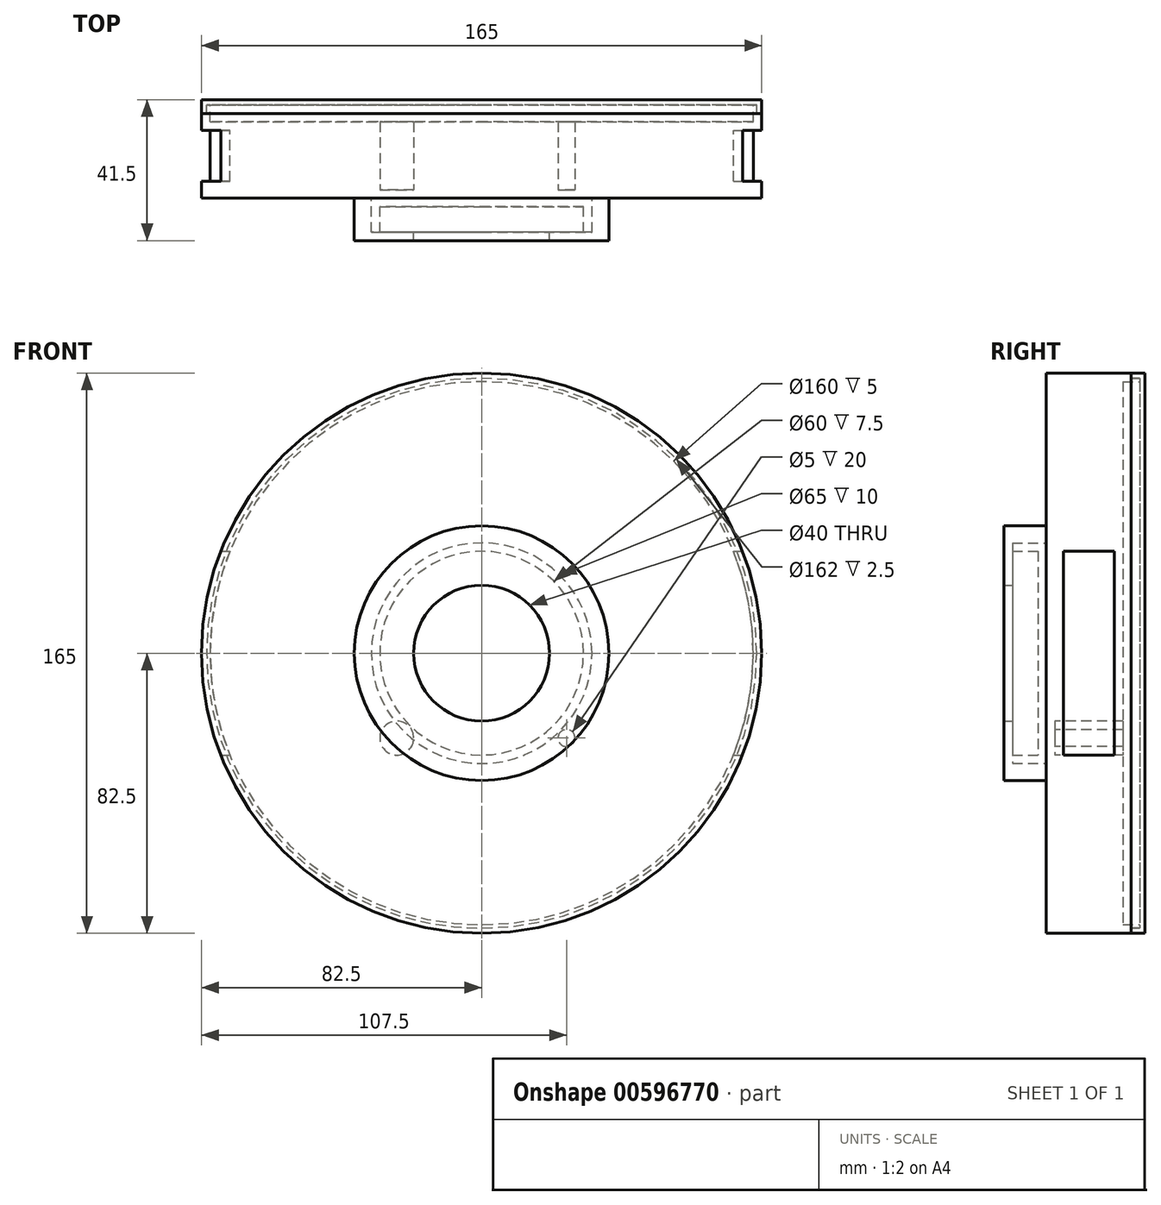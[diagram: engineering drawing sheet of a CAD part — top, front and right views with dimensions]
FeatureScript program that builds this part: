
annotation { "Feature Type Name" : "Feature", "Feature Type Description" : "" }
export const myFeature = defineFeature(function(context is Context, id is Id, definition is map)
    precondition{}
    {
        {
            var Q0;
            Q0=qCreatedBy(makeId("Right.planeOp"),FACE);
            var sketch = newSketch(context, id + "F0", { "sketchPlane" : qUnion([Q0])});
            skLineSegment(sketch, "E0.bottom", {"start": v(0, 0) * mm, "end": v(-2.5, 0) * mm});
            skLineSegment(sketch, "E0.top", {"start": v(0, 32.5) * mm, "end": v(-10, 32.5) * mm});
            skLineSegment(sketch, "E1", {"start": v(0, 0) * mm, "end": v(-55.69, 0) * mm, "construction": true});
            skLineSegment(sketch, "E2", {"start": v(-2.5, 0) * mm, "end": v(-2.5, 30) * mm});
            skLineSegment(sketch, "E3", {"start": v(-2.5, 30) * mm, "end": v(-10, 30) * mm});
            skLineSegment(sketch, "E4", {"start": v(-10, 30) * mm, "end": v(-10, 32.5) * mm});
            skLineSegment(sketch, "E5", {"start": v(0, 32.5) * mm, "end": v(0, 82.5) * mm});
            skLineSegment(sketch, "E6", {"start": v(0, 82.5) * mm, "end": v(25, 82.5) * mm});
            skLineSegment(sketch, "E7", {"start": v(25, 80) * mm, "end": v(2.5, 80) * mm});
            skLineSegment(sketch, "E8", {"start": v(2.5, 80) * mm, "end": v(2.5, 0) * mm});
            skLineSegment(sketch, "E9", {"start": v(2.5, 0) * mm, "end": v(-2.5, 0) * mm});
            skLineSegment(sketch, "E10", {"start": v(25, 80) * mm, "end": v(27.5, 80) * mm});
            skLineSegment(sketch, "E11", {"start": v(27.5, 80) * mm, "end": v(27.5, 81) * mm});
            skLineSegment(sketch, "E12", {"start": v(27.5, 81) * mm, "end": v(25, 81) * mm});
            skLineSegment(sketch, "E13", {"start": v(25, 81) * mm, "end": v(25, 82.5) * mm});
            skSolve(sketch);
        }
        {
            var Q0;
            Q0=qCreatedBy(makeId("Right.planeOp"),FACE);
            var sketch = newSketch(context, id + "F1", { "sketchPlane" : qUnion([Q0])});
            skLineSegment(sketch, "E14", {"start": v(0, 32.5) * mm, "end": v(-10, 32.5) * mm});
            skLineSegment(sketch, "E15", {"start": v(-10, 32.5) * mm, "end": v(-10, 20) * mm});
            skLineSegment(sketch, "E16", {"start": v(-10, 20) * mm, "end": v(-12.5, 20) * mm});
            skLineSegment(sketch, "E17", {"start": v(-12.5, 20) * mm, "end": v(-12.5, 37.5) * mm});
            skLineSegment(sketch, "E18", {"start": v(-12.5, 37.5) * mm, "end": v(0, 37.5) * mm});
            skLineSegment(sketch, "E19", {"start": v(0, 37.5) * mm, "end": v(0, 32.5) * mm});
            skLineSegment(sketch, "E20", {"start": v(0, 0) * mm, "end": v(-84.01, 0) * mm, "construction": true});
            skSolve(sketch);
        }
        {
            var Q0;
            Q0=qCreatedBy(makeId("Right.planeOp"),FACE);
            var sketch = newSketch(context, id + "F2", { "sketchPlane" : qUnion([Q0])});
            skLineSegment(sketch, "E21.bottom", {"start": v(-2.5, 0) * mm, "end": v(-10, 0) * mm});
            skLineSegment(sketch, "E21.top", {"start": v(-2.5, 30) * mm, "end": v(-10, 30) * mm});
            skLineSegment(sketch, "E21.left", {"start": v(-2.5, 0) * mm, "end": v(-2.5, 30) * mm});
            skLineSegment(sketch, "E21.right", {"start": v(-10, 0) * mm, "end": v(-10, 30) * mm});
            skSolve(sketch);
        }
        {
            var Q0;
            Q0=qCreatedBy(makeId("Right.planeOp"),FACE);
            var sketch = newSketch(context, id + "F3", { "sketchPlane" : qUnion([Q0])});
            skLineSegment(sketch, "E22", {"start": v(27.5, 0) * mm, "end": v(27.5, 79.3) * mm});
            skLineSegment(sketch, "E23", {"start": v(27.5, 79.3) * mm, "end": v(27.5, 81) * mm});
            skLineSegment(sketch, "E24", {"start": v(25, 82.5) * mm, "end": v(25, 81) * mm});
            skLineSegment(sketch, "E25", {"start": v(25, 81) * mm, "end": v(27.5, 81) * mm});
            skLineSegment(sketch, "E26", {"start": v(25, 82.5) * mm, "end": v(29, 82.5) * mm});
            skLineSegment(sketch, "E27", {"start": v(29, 82.5) * mm, "end": v(29, 0) * mm});
            skLineSegment(sketch, "E28", {"start": v(0, 0) * mm, "end": v(36.98, 0) * mm, "construction": true});
            skLineSegment(sketch, "E29", {"start": v(27.5, 0) * mm, "end": v(29, 0) * mm});
            skSolve(sketch);
        }
        {
            var Q0;
            Q0=makeQuery(id+"F0.imprint","IMPRINT",FACE,{"disambiguationData":[TD([[makeQuery(id+"F0.imprint","IMPRINT",EDGE,{"derivedFrom":sQuery(id+"F0.wireOp",EDGE,"E0.top")}),1.0]])]});
            var Q1;
            Q1=sQuery(id+"F0.wireOp",EDGE,"E0.top");
            var Q2;
            Q2=sQuery(id+"F0.wireOp",EDGE,"E0.bottom");
            var Q3;
            Q3=sQuery(id+"F0.wireOp",EDGE,"E0.right");
            var Q4;
            Q4=sQuery(id+"F0.wireOp",EDGE,"E0.left");
            var Q5;
            Q5=sQuery(id+"F0.wireOp",EDGE,"E1");
            revolve(context, id + "F4", {"entities" : qUnion([Q0]), "surfaceEntities" : qUnion([Q1, Q2, Q3, Q4]), "axis" : qUnion([Q5]), "revolveType" : RevolveType.FULL});
        }
        {
            var Q0;
            Q0=makeQuery(id+"F1.imprint","IMPRINT",FACE,{"disambiguationData":[TD([[makeQuery(id+"F1.imprint","IMPRINT",EDGE,{"derivedFrom":sQuery(id+"F1.wireOp",EDGE,"E14")}),-1.0]])]});
            var Q1;
            Q1=sQuery(id+"F1.wireOp",EDGE,"E20");
            revolve(context, id + "F5", {"entities" : qUnion([Q0]), "axis" : qUnion([Q1]), "revolveType" : RevolveType.FULL});
        }
        {
            var Q0;
            Q0 = qSketchRegion(id + "F3", true);
            var Q1;
            Q1=sQuery(id+"F3.wireOp",EDGE,"E27");
            var Q2;
            Q2=sQuery(id+"F3.wireOp",EDGE,"E22");
            var Q3;
            Q3=sQuery(id+"F3.wireOp",EDGE,"E26");
            var Q4;
            Q4=sQuery(id+"F3.wireOp",EDGE,"E25");
            var Q5;
            Q5=sQuery(id+"F3.wireOp",EDGE,"E24");
            var Q6;
            Q6=sQuery(id+"F3.wireOp",EDGE,"E23");
            var Q7;
            Q7=sQuery(id+"F3.wireOp",EDGE,"E28");
            revolve(context, id + "F6", {"entities" : qUnion([Q0]), "surfaceEntities" : qUnion([Q1, Q2, Q3, Q4, Q5, Q6]), "axis" : qUnion([Q7]), "revolveType" : RevolveType.FULL});
        }
        {
            var Q0;
            Q0 = qSketchRegion(id + "F2", true);
            var Q1;
            Q1=sQuery(id+"F0.wireOp",EDGE,"E1");
            revolve(context, id + "F7", {"entities" : qUnion([Q0]), "axis" : qUnion([Q1]), "revolveType" : RevolveType.FULL});
        }
        {
            var Q0;
            Q0=qCreatedBy(makeId("Right.planeOp"),FACE);
            var sketch = newSketch(context, id + "F8", { "sketchPlane" : qUnion([Q0])});
            skLineSegment(sketch, "E30.bottom", {"start": v(5, 30) * mm, "end": v(20, 30) * mm});
            skLineSegment(sketch, "E30.top", {"start": v(5, -30) * mm, "end": v(20, -30) * mm});
            skLineSegment(sketch, "E30.left", {"start": v(5, 30) * mm, "end": v(5, -30) * mm});
            skLineSegment(sketch, "E30.right", {"start": v(20, 30) * mm, "end": v(20, -30) * mm});
            skSolve(sketch);
        }
        {
            var Q0;
            Q0=makeQuery(id+"F8.imprint","IMPRINT",FACE,{"disambiguationData":[TD([[makeQuery(id+"F8.imprint","IMPRINT",EDGE,{"derivedFrom":sQuery(id+"F8.wireOp",EDGE,"E30.bottom")}),-1.0]])]});
            extrude(context, id + "F9", {"entities" : qUnion([Q0]), "operationType" : NewBodyOperationType.REMOVE, "endBound" : BoundingType.THROUGH_ALL, "oppositeDirection" : true, "depth" : 25 * mm, "offsetDistance" : 25 * mm, "hasSecondDirection" : true, "secondDirectionBound" : SecondDirectionBoundingType.THROUGH_ALL, "secondDirectionOppositeDirection" : false, "secondDirectionDepth" : 25 * mm});
        }
        {
            var Q0;
            Q0=makeQuery(id+"F4.opRevolve","SWEPT_FACE",FACE,{"disambiguationData":[OSD([sQuery(id+"F0.wireOp",EDGE,"E8")])]});
            var sketch = newSketch(context, id + "F10", { "sketchPlane" : qUnion([Q0])});
            skLineSegment(sketch, "E31", {"start": v(0, 0) * mm, "end": v(0, 62.68) * mm, "construction": true});
            skLineSegment(sketch, "E32", {"start": v(58.23, 0) * mm, "end": v(-68.44, 0) * mm, "construction": true});
            skCircle(sketch, "E33", {"center": v(-25, -25) * mm, "radius": 5 * mm});
            skCircle(sketch, "E34", {"center": v(-25, -25) * mm, "radius": 2.5 * mm});
            skCircle(sketch, "E35.MirrorC", {"center": v(25, -25) * mm, "radius": 5 * mm});
            skCircle(sketch, "E36.MirrorC", {"center": v(25, -25) * mm, "radius": 2.5 * mm});
            skSolve(sketch);
        }
        {
            var Q0;
            Q0=makeQuery(id+"F10.imprint","IMPRINT",FACE,{"disambiguationData":[TD([[makeQuery(id+"F10.imprint","IMPRINT",EDGE,{"derivedFrom":sQuery(id+"F10.wireOp",EDGE,"E33")}),1.0]])]});
            var Q1;
            Q1=makeQuery(id+"F10.imprint","IMPRINT",FACE,{"disambiguationData":[TD([[makeQuery(id+"F10.imprint","IMPRINT",EDGE,{"derivedFrom":sQuery(id+"F10.wireOp",EDGE,"E35.MirrorC")}),-1.0]])]});
            extrude(context, id + "F11", {"entities" : qUnion([Q0, Q1]), "operationType" : NewBodyOperationType.ADD, "depth" : 20 * mm, "offsetDistance" : 25 * mm});
        }
    });
